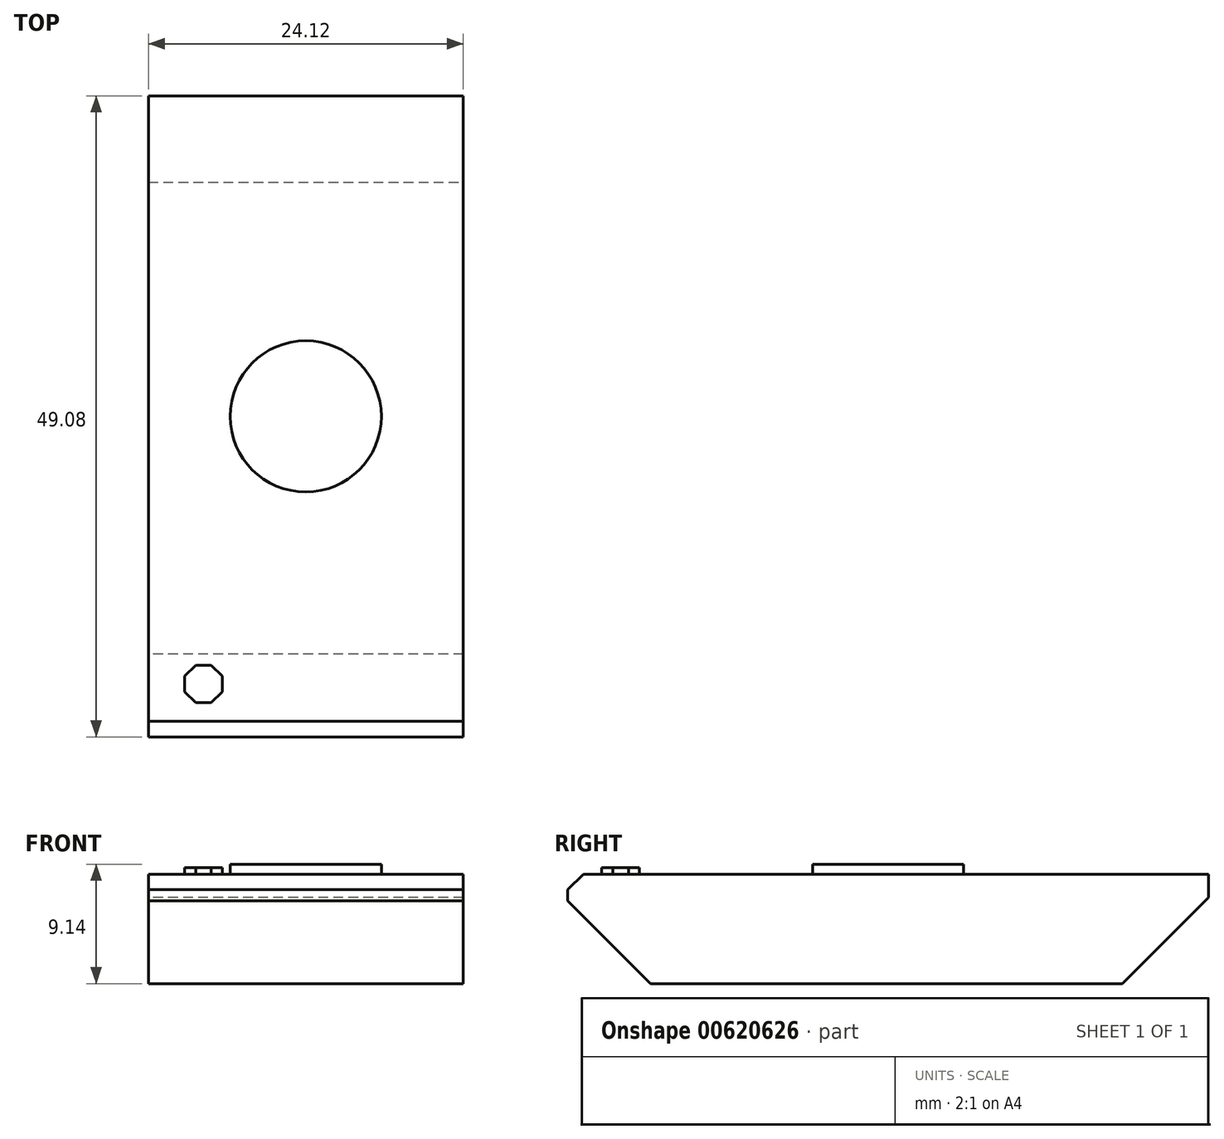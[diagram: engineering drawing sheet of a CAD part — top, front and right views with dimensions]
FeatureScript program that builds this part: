
annotation { "Feature Type Name" : "Feature", "Feature Type Description" : "" }
export const myFeature = defineFeature(function(context is Context, id is Id, definition is map)
    precondition{}
    {
        {
            var Q0;
            Q0=qCreatedBy(makeId("Top.planeOp"),FACE);
            var sketch = newSketch(context, id + "F0", { "sketchPlane" : qUnion([Q0])});
            skLineSegment(sketch, "E0.bottom", {"start": v(12.06, -24.54) * mm, "end": v(-12.06, -24.54) * mm});
            skLineSegment(sketch, "E0.top", {"start": v(12.06, 24.54) * mm, "end": v(-12.06, 24.54) * mm});
            skLineSegment(sketch, "E0.left", {"start": v(12.06, -24.54) * mm, "end": v(12.06, 24.54) * mm});
            skLineSegment(sketch, "E0.right", {"start": v(-12.06, -24.54) * mm, "end": v(-12.06, 24.54) * mm});
            skPoint(sketch, "E0.middle", {"position": v(0, 0) * mm});
            skSolve(sketch);
        }
        {
            var Q0;
            Q0=makeQuery(id+"F0.imprint","IMPRINT",FACE,{"disambiguationData":[TD([[makeQuery(id+"F0.imprint","IMPRINT",EDGE,{"derivedFrom":sQuery(id+"F0.wireOp",EDGE,"E0.bottom")}),-1.0]])]});
            extrude(context, id + "F1", {"entities" : qUnion([Q0]), "depth" : 8.38 * mm, "offsetDistance" : 25.4 * mm});
        }
        {
            var Q0;
            Q0=makeQuery(id+"F1.opExtrude","CAP_EDGE",EDGE,{"disambiguationData":[OSD([sQuery(id+"F0.wireOp",EDGE,"E0.bottom")])],"isStart":true});
            chamfer(context, id + "F2", {"entities" : qUnion([Q0]), "width" : 6.35 * mm, "tangentPropagation" : true});
        }
        {
            var Q0;
            Q0=makeQuery(id+"F1.opExtrude","CAP_EDGE",EDGE,{"disambiguationData":[OSD([sQuery(id+"F0.wireOp",EDGE,"E0.top")])],"isStart":true});
            chamfer(context, id + "F3", {"entities" : qUnion([Q0]), "width" : 6.6 * mm, "tangentPropagation" : true});
        }
        {
            var Q0;
            Q0=qCreatedBy(makeId("Top.planeOp"),FACE);
            var sketch = newSketch(context, id + "F4", { "sketchPlane" : qUnion([Q0])});
            skCircle(sketch, "E1", {"center": v(0, 0) * mm, "radius": 5.79 * mm});
            skSolve(sketch);
        }
        {
            var Q0;
            Q0=makeQuery(id+"F4.imprint","IMPRINT",FACE,{"disambiguationData":[TD([[makeQuery(id+"F4.imprint","IMPRINT",EDGE,{"derivedFrom":sQuery(id+"F4.wireOp",EDGE,"E1")}),1.0]])]});
            var Q1;
            Q1=sQuery(id+"F4.wireOp",EDGE,"E1");
            extrude(context, id + "F5", {"entities" : qUnion([Q0]), "operationType" : NewBodyOperationType.ADD, "surfaceEntities" : qUnion([Q1]), "depth" : 9.14 * mm, "offsetDistance" : 25.4 * mm});
        }
        {
            var Q0;
            Q0=makeQuery(id+"F1.opExtrude","CAP_FACE",FACE,{"disambiguationData":[OSD([sQuery(id+"F0.wireOp",EDGE,"E0.bottom"),sQuery(id+"F0.wireOp",EDGE,"E0.top"),sQuery(id+"F0.wireOp",EDGE,"E0.left"),sQuery(id+"F0.wireOp",EDGE,"E0.right")])],"isStart":false});
            var sketch = newSketch(context, id + "F6", { "sketchPlane" : qUnion([Q0])});
            skCircle(sketch, "E2.cCircle", {"center": v(-7.84, -20.49) * mm, "radius": 1.44 * mm, "construction": true});
            skLineSegment(sketch, "E2.0", {"start": v(-7.24, -21.93) * mm, "end": v(-8.43, -21.93) * mm});
            skLineSegment(sketch, "E2.1", {"start": v(-8.43, -21.93) * mm, "end": v(-9.28, -21.09) * mm});
            skLineSegment(sketch, "E2.2", {"start": v(-9.28, -21.09) * mm, "end": v(-9.28, -19.9) * mm});
            skLineSegment(sketch, "E2.3", {"start": v(-9.28, -19.9) * mm, "end": v(-8.43, -19.05) * mm});
            skLineSegment(sketch, "E2.4", {"start": v(-8.43, -19.05) * mm, "end": v(-7.24, -19.05) * mm});
            skLineSegment(sketch, "E2.5", {"start": v(-7.24, -19.05) * mm, "end": v(-6.4, -19.9) * mm});
            skLineSegment(sketch, "E2.6", {"start": v(-6.4, -19.9) * mm, "end": v(-6.4, -21.09) * mm});
            skLineSegment(sketch, "E2.7", {"start": v(-6.4, -21.09) * mm, "end": v(-7.24, -21.93) * mm});
            skPoint(sketch, "E2.0.midPoint", {"position": v(-7.84, -21.93) * mm});
            skSolve(sketch);
        }
        {
            var Q0;
            Q0=makeQuery(id+"F6.imprint","IMPRINT",FACE,{"disambiguationData":[TD([[makeQuery(id+"F6.imprint","IMPRINT",EDGE,{"derivedFrom":sQuery(id+"F6.wireOp",EDGE,"E2.0")}),-1.0]])]});
            extrude(context, id + "F7", {"entities" : qUnion([Q0]), "operationType" : NewBodyOperationType.ADD, "depth" : 0.5 * mm, "offsetDistance" : 25.4 * mm});
        }
        {
            var Q0;
            Q0=makeQuery(id+"F1.opExtrude","CAP_EDGE",EDGE,{"disambiguationData":[OSD([sQuery(id+"F0.wireOp",EDGE,"E0.bottom")])],"isStart":false});
            chamfer(context, id + "F8", {"entities" : qUnion([Q0]), "width" : 1.2 * mm, "tangentPropagation" : true});
        }
    });
